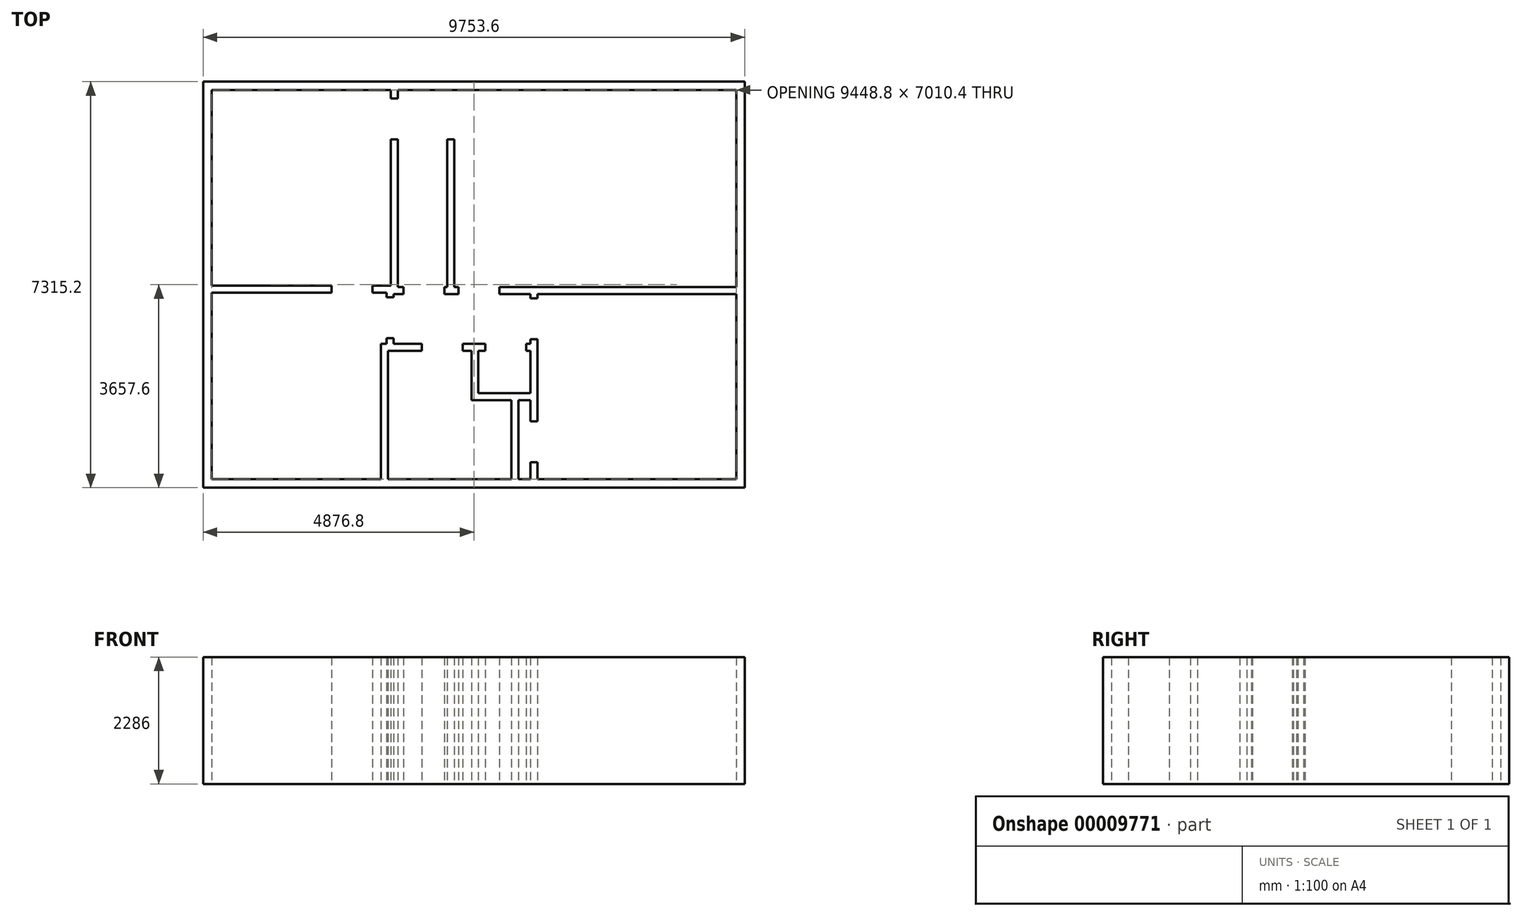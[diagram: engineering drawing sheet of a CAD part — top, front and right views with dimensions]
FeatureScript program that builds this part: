
annotation { "Feature Type Name" : "Feature", "Feature Type Description" : "" }
export const myFeature = defineFeature(function(context is Context, id is Id, definition is map)
    precondition{}
    {
        {
            var Q0;
            Q0=qCreatedBy(makeId("Top.planeOp"),FACE);
            var sketch = newSketch(context, id + "F0", { "sketchPlane" : qUnion([Q0])});
            skLineSegment(sketch, "E0.bottom", {"start": v(0, 0) * mm, "end": v(9753.6, 0) * mm});
            skLineSegment(sketch, "E0.top", {"start": v(0, 7315.2) * mm, "end": v(9753.6, 7315.2) * mm});
            skLineSegment(sketch, "E0.left", {"start": v(0, 0) * mm, "end": v(0, 7315.2) * mm});
            skLineSegment(sketch, "E0.right", {"start": v(9753.6, 0) * mm, "end": v(9753.6, 7315.2) * mm});
            skSolve(sketch);
        }
        {
            var Q0;
            Q0=makeQuery(id+"F0.imprint","IMPRINT",FACE,{"disambiguationData":[TD([[makeQuery(id+"F0.imprint","IMPRINT",EDGE,{"derivedFrom":sQuery(id+"F0.wireOp",EDGE,"E0.bottom")}),1.0]])]});
            var sketch = newSketch(context, id + "F1", { "sketchPlane" : qUnion([Q0])});
            skLineSegment(sketch, "E1.0", {"start": v(0, 7315.2) * mm, "end": v(9753.6, 7315.2) * mm});
            skLineSegment(sketch, "E2.0", {"start": v(9753.6, 0) * mm, "end": v(9753.6, 7315.2) * mm});
            skLineSegment(sketch, "E3.0", {"start": v(0, 0) * mm, "end": v(9753.6, 0) * mm});
            skLineSegment(sketch, "E4", {"start": v(3505.2, 7162.8) * mm, "end": v(9601.2, 7162.8) * mm});
            skLineSegment(sketch, "E5", {"start": v(9601.2, 7162.8) * mm, "end": v(9601.2, 3616.76) * mm});
            skLineSegment(sketch, "E6", {"start": v(9601.2, 3616.76) * mm, "end": v(5334, 3616.76) * mm});
            skLineSegment(sketch, "E7", {"start": v(5334, 3616.76) * mm, "end": v(5334, 3489.66) * mm});
            skLineSegment(sketch, "E8", {"start": v(5334, 3489.66) * mm, "end": v(5892.7, 3489.66) * mm});
            skLineSegment(sketch, "E9", {"start": v(5892.7, 3489.66) * mm, "end": v(5892.7, 3413.46) * mm});
            skLineSegment(sketch, "E10", {"start": v(5892.7, 3413.46) * mm, "end": v(6019.8, 3413.46) * mm});
            skLineSegment(sketch, "E11", {"start": v(6019.8, 3413.46) * mm, "end": v(6019.8, 3489.66) * mm});
            skLineSegment(sketch, "E12", {"start": v(6019.8, 3489.66) * mm, "end": v(9601.2, 3489.66) * mm});
            skLineSegment(sketch, "E13", {"start": v(9601.2, 3489.66) * mm, "end": v(9601.2, 152.4) * mm});
            skLineSegment(sketch, "E14", {"start": v(9601.2, 152.4) * mm, "end": v(6019.8, 152.4) * mm});
            skLineSegment(sketch, "E15", {"start": v(6019.8, 152.4) * mm, "end": v(6019.8, 457.2) * mm});
            skLineSegment(sketch, "E16", {"start": v(6019.8, 457.2) * mm, "end": v(5892.7, 457.2) * mm});
            skLineSegment(sketch, "E17", {"start": v(5892.7, 457.2) * mm, "end": v(5892.7, 152.4) * mm});
            skLineSegment(sketch, "E18", {"start": v(5892.7, 152.4) * mm, "end": v(5678.73, 152.4) * mm});
            skLineSegment(sketch, "E19", {"start": v(5678.73, 152.4) * mm, "end": v(5678.73, 1574.57) * mm});
            skLineSegment(sketch, "E20", {"start": v(5678.73, 1574.57) * mm, "end": v(5892.7, 1574.57) * mm});
            skLineSegment(sketch, "E21", {"start": v(5892.7, 1574.57) * mm, "end": v(5892.7, 1193.8) * mm});
            skLineSegment(sketch, "E22", {"start": v(5892.7, 1193.8) * mm, "end": v(6019.8, 1193.8) * mm});
            skLineSegment(sketch, "E23", {"start": v(6019.8, 1193.8) * mm, "end": v(6019.8, 2676.75) * mm});
            skLineSegment(sketch, "E24", {"start": v(6019.8, 2676.75) * mm, "end": v(5892.7, 2676.75) * mm});
            skLineSegment(sketch, "E25", {"start": v(5892.7, 2676.75) * mm, "end": v(5892.7, 2590.8) * mm});
            skLineSegment(sketch, "E26", {"start": v(5892.7, 2590.8) * mm, "end": v(5816.5, 2590.8) * mm});
            skLineSegment(sketch, "E27", {"start": v(5816.5, 2590.8) * mm, "end": v(5816.5, 2463.7) * mm});
            skLineSegment(sketch, "E28", {"start": v(5816.5, 2463.7) * mm, "end": v(5892.7, 2463.7) * mm});
            skLineSegment(sketch, "E29", {"start": v(5892.7, 2463.7) * mm, "end": v(5892.7, 1701.67) * mm});
            skLineSegment(sketch, "E30", {"start": v(5892.7, 1701.67) * mm, "end": v(4957.57, 1701.67) * mm});
            skLineSegment(sketch, "E31", {"start": v(4957.57, 1701.67) * mm, "end": v(4957.57, 2463.7) * mm});
            skLineSegment(sketch, "E32", {"start": v(4957.57, 2463.7) * mm, "end": v(5079.8, 2463.7) * mm});
            skLineSegment(sketch, "E33", {"start": v(5079.8, 2463.7) * mm, "end": v(5079.8, 2590.8) * mm});
            skLineSegment(sketch, "E34", {"start": v(5079.8, 2590.8) * mm, "end": v(4673.8, 2590.8) * mm});
            skLineSegment(sketch, "E35", {"start": v(4673.8, 2590.8) * mm, "end": v(4673.8, 2463.7) * mm});
            skLineSegment(sketch, "E36", {"start": v(4673.8, 2463.7) * mm, "end": v(4830.47, 2463.7) * mm});
            skLineSegment(sketch, "E37", {"start": v(4830.47, 2463.7) * mm, "end": v(4830.47, 1574.57) * mm});
            skLineSegment(sketch, "E38", {"start": v(4830.47, 1574.57) * mm, "end": v(5551.63, 1574.57) * mm});
            skLineSegment(sketch, "E39", {"start": v(5551.63, 1574.57) * mm, "end": v(5551.63, 152.4) * mm});
            skLineSegment(sketch, "E40", {"start": v(5551.63, 152.4) * mm, "end": v(3327.5, 152.4) * mm});
            skLineSegment(sketch, "E41", {"start": v(3327.5, 152.4) * mm, "end": v(3327.5, 2463.7) * mm});
            skLineSegment(sketch, "E42", {"start": v(3327.5, 2463.7) * mm, "end": v(3937.1, 2463.7) * mm});
            skLineSegment(sketch, "E43", {"start": v(3937.1, 2463.7) * mm, "end": v(3937.1, 2590.8) * mm});
            skLineSegment(sketch, "E44", {"start": v(3937.1, 2590.8) * mm, "end": v(3428.09, 2590.8) * mm});
            skLineSegment(sketch, "E45", {"start": v(3428.09, 2590.8) * mm, "end": v(3428.09, 2691.38) * mm});
            skLineSegment(sketch, "E46", {"start": v(3428.09, 2691.38) * mm, "end": v(3300.98, 2691.38) * mm});
            skLineSegment(sketch, "E47", {"start": v(3300.98, 2691.38) * mm, "end": v(3300.98, 2590.8) * mm});
            skLineSegment(sketch, "E48", {"start": v(3300.98, 2590.8) * mm, "end": v(3200.4, 2590.8) * mm});
            skLineSegment(sketch, "E49", {"start": v(3200.4, 2590.8) * mm, "end": v(3200.4, 152.4) * mm});
            skLineSegment(sketch, "E50", {"start": v(3200.4, 152.4) * mm, "end": v(152.4, 152.4) * mm});
            skLineSegment(sketch, "E51", {"start": v(152.4, 152.4) * mm, "end": v(152.4, 3515.06) * mm});
            skLineSegment(sketch, "E52", {"start": v(152.4, 3515.06) * mm, "end": v(2311.6, 3515.06) * mm});
            skLineSegment(sketch, "E53", {"start": v(2311.6, 3515.06) * mm, "end": v(2311.6, 3642.06) * mm});
            skLineSegment(sketch, "E54", {"start": v(2311.6, 3642.06) * mm, "end": v(152.4, 3642.06) * mm});
            skLineSegment(sketch, "E55", {"start": v(152.4, 3642.06) * mm, "end": v(152.4, 7162.8) * mm});
            skLineSegment(sketch, "E56", {"start": v(152.4, 7162.8) * mm, "end": v(3378.1, 7162.8) * mm});
            skLineSegment(sketch, "E57", {"start": v(3378.1, 7162.8) * mm, "end": v(3378.1, 7010.4) * mm});
            skLineSegment(sketch, "E58", {"start": v(3378.1, 7010.4) * mm, "end": v(3505.2, 7010.4) * mm});
            skLineSegment(sketch, "E59", {"start": v(3505.2, 7010.4) * mm, "end": v(3505.2, 7162.8) * mm});
            skLineSegment(sketch, "E60", {"start": v(3378.1, 6273.7) * mm, "end": v(3378.1, 3642.06) * mm});
            skLineSegment(sketch, "E61", {"start": v(3378.1, 3642.06) * mm, "end": v(3048.3, 3642.06) * mm});
            skLineSegment(sketch, "E62", {"start": v(3048.3, 3642.06) * mm, "end": v(3048.3, 3515.06) * mm});
            skLineSegment(sketch, "E63", {"start": v(3048.3, 3515.06) * mm, "end": v(3300.98, 3515.06) * mm});
            skLineSegment(sketch, "E64", {"start": v(3300.98, 3515.06) * mm, "end": v(3300.98, 3428.09) * mm});
            skLineSegment(sketch, "E65", {"start": v(3300.98, 3428.09) * mm, "end": v(3428.09, 3428.09) * mm});
            skLineSegment(sketch, "E66", {"start": v(3428.09, 3428.09) * mm, "end": v(3428.09, 3489.66) * mm});
            skLineSegment(sketch, "E67", {"start": v(3428.09, 3489.66) * mm, "end": v(3605.78, 3489.66) * mm});
            skLineSegment(sketch, "E68", {"start": v(3605.78, 3489.66) * mm, "end": v(3605.78, 3616.76) * mm});
            skLineSegment(sketch, "E69", {"start": v(3605.78, 3616.76) * mm, "end": v(3505.2, 3616.76) * mm});
            skLineSegment(sketch, "E70", {"start": v(3505.2, 3616.76) * mm, "end": v(3505.2, 6273.7) * mm});
            skLineSegment(sketch, "E71", {"start": v(3505.2, 6273.7) * mm, "end": v(3378.1, 6273.7) * mm});
            skLineSegment(sketch, "E72", {"start": v(4394.3, 6273.7) * mm, "end": v(4394.3, 3616.76) * mm});
            skLineSegment(sketch, "E73", {"start": v(4394.3, 3616.76) * mm, "end": v(4342.49, 3616.76) * mm});
            skLineSegment(sketch, "E74", {"start": v(4342.49, 3616.76) * mm, "end": v(4342.49, 3489.66) * mm});
            skLineSegment(sketch, "E75", {"start": v(4342.49, 3489.66) * mm, "end": v(4597.3, 3489.66) * mm});
            skLineSegment(sketch, "E76", {"start": v(4597.3, 3489.66) * mm, "end": v(4597.3, 3616.76) * mm});
            skLineSegment(sketch, "E77", {"start": v(4597.3, 3616.76) * mm, "end": v(4521.4, 3616.76) * mm});
            skLineSegment(sketch, "E78", {"start": v(4521.4, 3616.76) * mm, "end": v(4521.4, 6273.7) * mm});
            skLineSegment(sketch, "E79", {"start": v(4521.4, 6273.7) * mm, "end": v(4394.3, 6273.7) * mm});
            skLineSegment(sketch, "E80.0", {"start": v(0, 0) * mm, "end": v(0, 7315.2) * mm});
            skSolve(sketch);
        }
        {
            var Q0;
            Q0=makeQuery(id+"F1.imprint","IMPRINT",FACE,{"disambiguationData":[TD([[makeQuery(id+"F1.imprint","IMPRINT",EDGE,{"derivedFrom":sQuery(id+"F1.wireOp",EDGE,"E1.0")}),-1.0]])]});
            var Q1;
            Q1=makeQuery(id+"F1.imprint","IMPRINT",FACE,{"disambiguationData":[TD([[makeQuery(id+"F1.imprint","IMPRINT",EDGE,{"derivedFrom":sQuery(id+"F1.wireOp",EDGE,"E60")}),1.0]])]});
            var Q2;
            Q2=makeQuery(id+"F1.imprint","IMPRINT",FACE,{"disambiguationData":[TD([[makeQuery(id+"F1.imprint","IMPRINT",EDGE,{"derivedFrom":sQuery(id+"F1.wireOp",EDGE,"E72")}),1.0]])]});
            extrude(context, id + "F2", {"entities" : qUnion([Q0, Q1, Q2]), "depth" : 2286 * mm});
        }
    });
